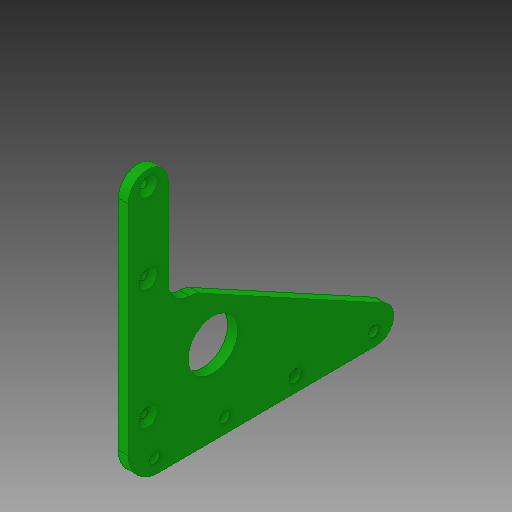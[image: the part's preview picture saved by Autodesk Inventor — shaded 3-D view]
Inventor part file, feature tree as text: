
AUTODESK INVENTOR PART (.ipt)
format: ipt  version: 2017 SP1 (Build 210196100, 196)  size: 151,552 bytes
history: native  units: in
note: dims shown in document units (in); Inventor stores cm internally (conversion verified against a paired STEP export)
features: extrude x1, chamfer x1
ambient origin geometry x8: Origin, YZ Plane, XZ Plane, XY Plane, X Axis, Y Axis, Z Axis, Center Point
bodies: Solid1 (feature_tree)
feature tree (2):
  extrude  "Extrusion1"  Depth=0.21in
  chamfer  "Chamfer1"  Distance=5.0in
